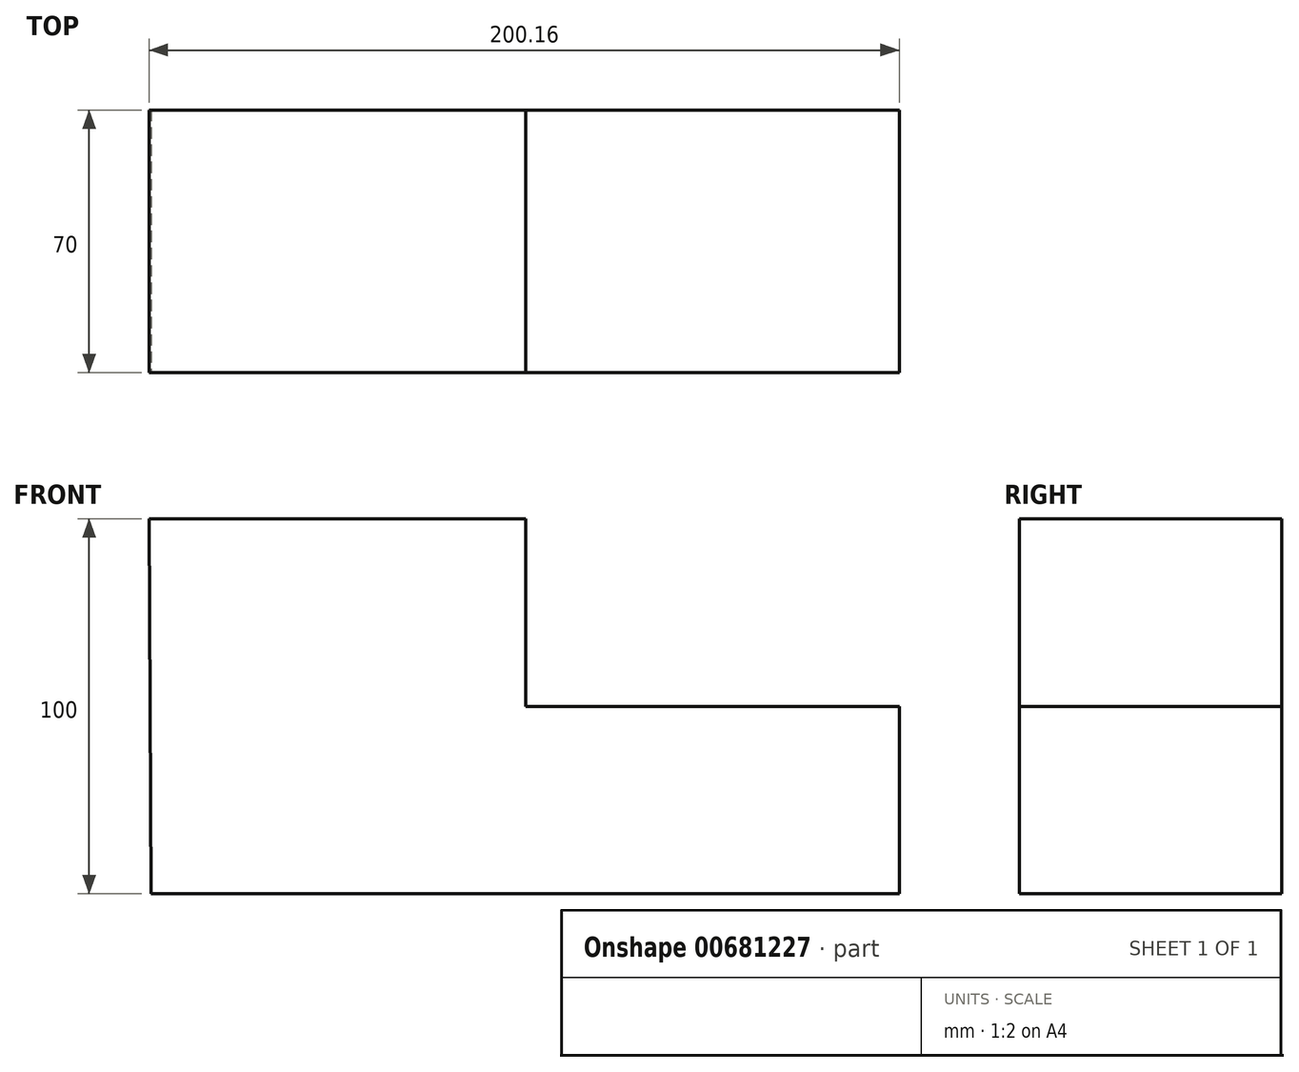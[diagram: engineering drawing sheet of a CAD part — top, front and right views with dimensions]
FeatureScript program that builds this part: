
annotation { "Feature Type Name" : "Feature", "Feature Type Description" : "" }
export const myFeature = defineFeature(function(context is Context, id is Id, definition is map)
    precondition{}
    {
        {
            var Q0;
            Q0=qCreatedBy(makeId("Front.planeOp"),FACE);
            var sketch = newSketch(context, id + "F0", { "sketchPlane" : qUnion([Q0])});
            skLineSegment(sketch, "E0", {"start": v(-100.48, 99.84) * mm, "end": v(0, 99.84) * mm});
            skLineSegment(sketch, "E1", {"start": v(0, 49.84) * mm, "end": v(99.68, 49.84) * mm});
            skLineSegment(sketch, "E2", {"start": v(99.68, 49.84) * mm, "end": v(99.68, -0.16) * mm});
            skLineSegment(sketch, "E3", {"start": v(99.68, -0.16) * mm, "end": v(-100, -0.16) * mm});
            skLineSegment(sketch, "E4", {"start": v(-100, -0.16) * mm, "end": v(-100.48, 99.84) * mm});
            skLineSegment(sketch, "E5", {"start": v(0, 99.84) * mm, "end": v(0, 49.84) * mm});
            skSolve(sketch);
        }
        {
            var Q0;
            Q0 = qSketchRegion(id + "F0", true);
            extrude(context, id + "F1", {"entities" : qUnion([Q0]), "oppositeDirection" : true, "depth" : 70 * mm, "offsetDistance" : 25 * mm});
        }
    });
